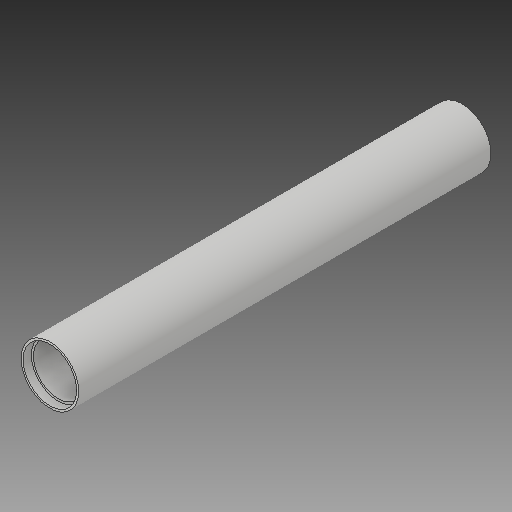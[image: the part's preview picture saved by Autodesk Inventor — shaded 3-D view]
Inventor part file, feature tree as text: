
AUTODESK INVENTOR PART (.ipt)
format: ipt  version: 2019 (Build 230136000, 136)  size: 98,816 bytes
history: native  units: in
note: dims shown in document units (in); Inventor stores cm internally (conversion verified against a paired STEP export)
features: sketch x4, other x3
ambient origin geometry x8: Origin, YZ Plane, XZ Plane, XY Plane, X Axis, Y Axis, Z Axis, Center Point
bodies: Solid1 (feature_tree)
feature tree (7):
  other  "project roller 2 part 2.ipt"
  other  "Solid1::project roller 2 part 2.ipt"
  other  "TaggingFeature1"
  sketch  "Sketch1"  dims[d0=0.3937in]
  sketch  "Sketch2"
  sketch  "Sketch3"
  sketch  "Sketch4"
